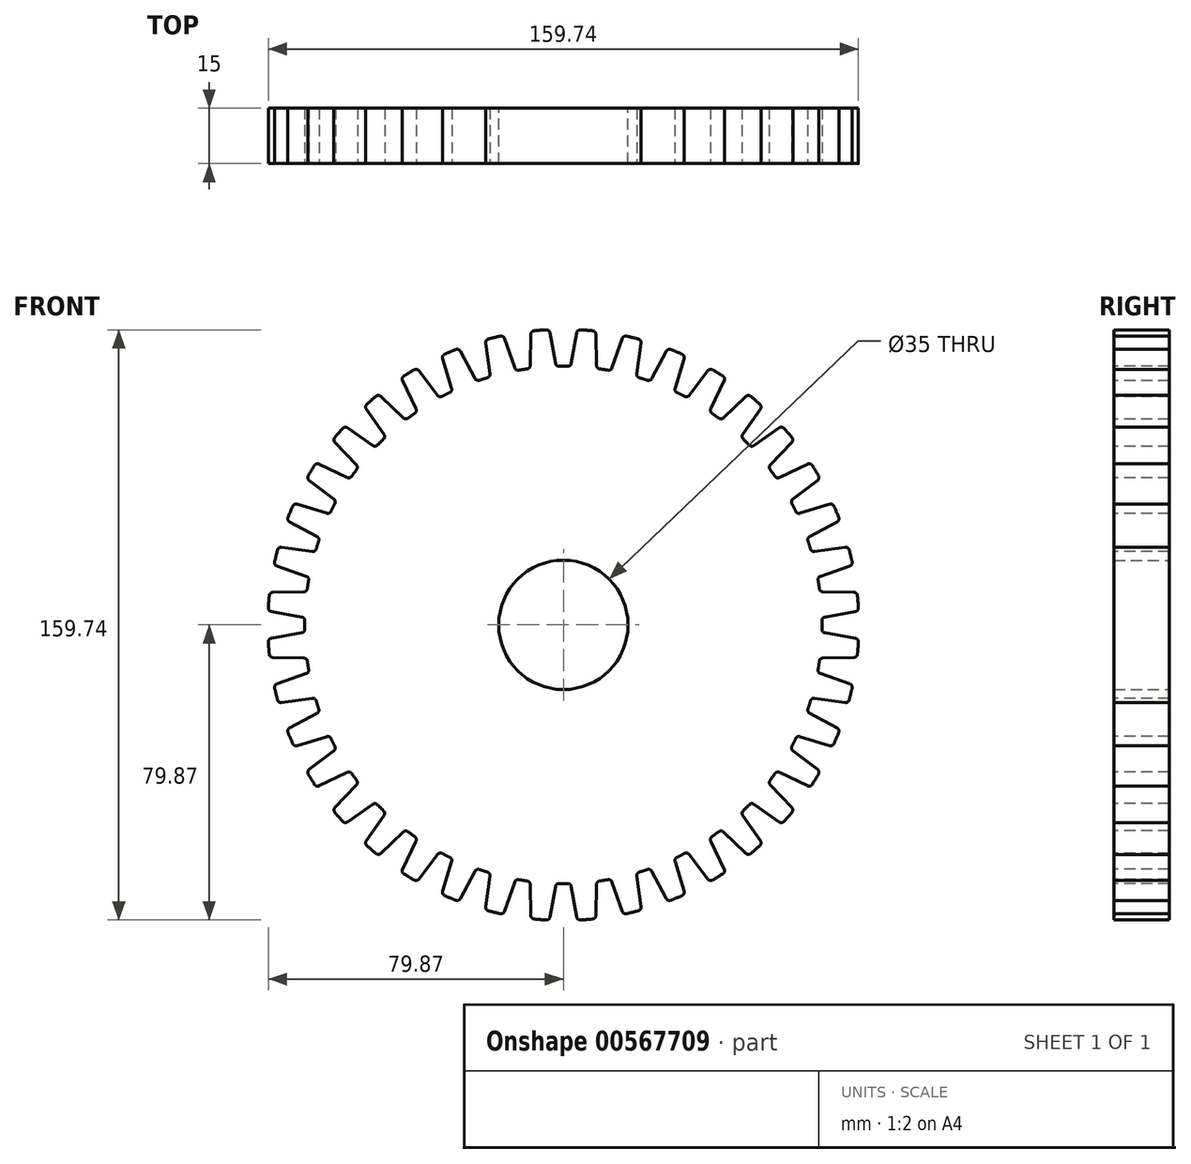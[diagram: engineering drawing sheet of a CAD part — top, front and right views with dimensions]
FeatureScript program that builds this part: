
annotation { "Feature Type Name" : "Feature", "Feature Type Description" : "" }
export const myFeature = defineFeature(function(context is Context, id is Id, definition is map)
    precondition{}
    {
        {
            var Q0;
            Q0=qCreatedBy(makeId("Front.planeOp"),FACE);
            var sketch = newSketch(context, id + "F0", { "sketchPlane" : qUnion([Q0])});
            skCircle(sketch, "E0", {"center": v(0, 0) * mm, "radius": 80 * mm});
            skCircle(sketch, "E1", {"center": v(0, 0) * mm, "radius": 17.5 * mm});
            skSolve(sketch);
        }
        {
            var Q0;
            Q0=makeQuery(id+"F0.imprint","IMPRINT",FACE,{"disambiguationData":[TD([[makeQuery(id+"F0.imprint","IMPRINT",EDGE,{"derivedFrom":sQuery(id+"F0.wireOp",EDGE,"E0")}),1.0]])]});
            extrude(context, id + "F1", {"entities" : qUnion([Q0]), "endBound" : BoundingType.SYMMETRIC, "depth" : 15 * mm, "offsetDistance" : 25 * mm});
        }
        {
            var Q0;
            Q0=qCreatedBy(makeId("Front.planeOp"),FACE);
            var sketch = newSketch(context, id + "F2", { "sketchPlane" : qUnion([Q0])});
            skLineSegment(sketch, "E2", {"start": v(0, 80) * mm, "end": v(0, 70) * mm});
            skArc(sketch, "E3", {"start": v(1.15, 70) * mm, "mid": v(0, 70) * mm, "end": v(-1.15, 70) * mm});
            skLineSegment(sketch, "E4", {"start": v(2.15, 70.82) * mm, "end": v(3.6, 79.04) * mm});
            skLineSegment(sketch, "E5.MirrorCS", {"start": v(-2.15, 70.82) * mm, "end": v(-3.6, 79.04) * mm});
            skPoint(sketch, "E6.orphan", {"position": v(-4.08, 81.74) * mm});
            skPoint(sketch, "E7.orphan", {"position": v(4.08, 81.74) * mm});
            skPoint(sketch, "E8.visualSharp", {"position": v(3.75, 79.91) * mm});
            skArc(sketch, "E8.filletArc", {"start": v(4.64, 79.87) * mm, "mid": v(3.96, 79.65) * mm, "end": v(3.6, 79.04) * mm});
            skPoint(sketch, "E9.visualSharp", {"position": v(-3.75, 79.91) * mm});
            skArc(sketch, "E9.filletArc", {"start": v(-3.6, 79.04) * mm, "mid": v(-3.96, 79.65) * mm, "end": v(-4.64, 79.87) * mm});
            skPoint(sketch, "E10.visualSharp", {"position": v(-2, 69.97) * mm});
            skArc(sketch, "E10.filletArc", {"start": v(-2.15, 70.82) * mm, "mid": v(-1.8, 70.22) * mm, "end": v(-1.15, 70) * mm});
            skPoint(sketch, "E11.visualSharp", {"position": v(2, 69.97) * mm});
            skArc(sketch, "E11.filletArc", {"start": v(1.15, 70) * mm, "mid": v(1.8, 70.22) * mm, "end": v(2.15, 70.82) * mm});
            skArc(sketch, "E12.converted", {"start": v(4.64, 79.87) * mm, "mid": v(0, 80) * mm, "end": v(-4.64, 79.87) * mm});
            skPoint(sketch, "E13.1.0", {"position": v(-16.81, 80.1) * mm});
            skPoint(sketch, "E13.1.1", {"position": v(-8.76, 81.37) * mm});
            skPoint(sketch, "E13.1.2", {"position": v(-12.92, 68.8) * mm});
            skPoint(sketch, "E13.1.3", {"position": v(-8.8, 79.52) * mm});
            skPoint(sketch, "E13.1.4", {"position": v(-16.2, 78.34) * mm});
            skLineSegment(sketch, "E13.1.5", {"start": v(-12.51, 79.02) * mm, "end": v(-10.95, 69.14) * mm});
            skPoint(sketch, "E13.1.6", {"position": v(-8.97, 69.42) * mm});
            skLineSegment(sketch, "E13.1.7", {"start": v(-8.96, 70.28) * mm, "end": v(-8.8, 78.63) * mm});
            skLineSegment(sketch, "E13.1.8", {"start": v(-13.2, 69.6) * mm, "end": v(-15.92, 77.5) * mm});
            skArc(sketch, "E13.1.9", {"start": v(-7.9, 79.6) * mm, "mid": v(-12.51, 79.02) * mm, "end": v(-17.08, 78.16) * mm});
            skArc(sketch, "E13.1.10", {"start": v(-9.82, 69.3) * mm, "mid": v(-10.95, 69.14) * mm, "end": v(-12.08, 68.95) * mm});
            skArc(sketch, "E13.1.11", {"start": v(-13.2, 69.6) * mm, "mid": v(-12.76, 69.07) * mm, "end": v(-12.08, 68.95) * mm});
            skArc(sketch, "E13.1.12", {"start": v(-9.82, 69.3) * mm, "mid": v(-9.2, 69.64) * mm, "end": v(-8.96, 70.28) * mm});
            skArc(sketch, "E13.1.13", {"start": v(-7.9, 79.6) * mm, "mid": v(-8.55, 79.3) * mm, "end": v(-8.8, 78.63) * mm});
            skArc(sketch, "E13.1.14", {"start": v(-15.92, 77.5) * mm, "mid": v(-16.38, 78.05) * mm, "end": v(-17.08, 78.16) * mm});
            skPoint(sketch, "E13.2.0", {"position": v(-29.14, 76.48) * mm});
            skPoint(sketch, "E13.2.1", {"position": v(-21.38, 79) * mm});
            skPoint(sketch, "E13.2.2", {"position": v(-23.52, 65.93) * mm});
            skPoint(sketch, "E13.2.3", {"position": v(-21.13, 77.16) * mm});
            skPoint(sketch, "E13.2.4", {"position": v(-28.26, 74.84) * mm});
            skLineSegment(sketch, "E13.2.5", {"start": v(-24.72, 76.08) * mm, "end": v(-21.63, 66.57) * mm});
            skPoint(sketch, "E13.2.6", {"position": v(-19.72, 67.16) * mm});
            skLineSegment(sketch, "E13.2.7", {"start": v(-19.84, 68.01) * mm, "end": v(-21, 76.28) * mm});
            skLineSegment(sketch, "E13.2.8", {"start": v(-23.93, 66.69) * mm, "end": v(-27.85, 74.06) * mm});
            skArc(sketch, "E13.2.9", {"start": v(-20.26, 77.4) * mm, "mid": v(-24.72, 76.08) * mm, "end": v(-29.1, 74.52) * mm});
            skArc(sketch, "E13.2.10", {"start": v(-20.54, 66.92) * mm, "mid": v(-21.63, 66.57) * mm, "end": v(-22.72, 66.21) * mm});
            skArc(sketch, "E13.2.11", {"start": v(-23.93, 66.69) * mm, "mid": v(-23.41, 66.23) * mm, "end": v(-22.72, 66.21) * mm});
            skArc(sketch, "E13.2.12", {"start": v(-20.54, 66.92) * mm, "mid": v(-19.99, 67.34) * mm, "end": v(-19.84, 68.01) * mm});
            skArc(sketch, "E13.2.13", {"start": v(-20.26, 77.4) * mm, "mid": v(-20.84, 76.98) * mm, "end": v(-21, 76.28) * mm});
            skArc(sketch, "E13.2.14", {"start": v(-27.85, 74.06) * mm, "mid": v(-28.38, 74.53) * mm, "end": v(-29.1, 74.52) * mm});
            skPoint(sketch, "E13.3.0", {"position": v(-40.74, 70.98) * mm});
            skPoint(sketch, "E13.3.1", {"position": v(-33.48, 74.68) * mm});
            skPoint(sketch, "E13.3.2", {"position": v(-33.55, 61.44) * mm});
            skPoint(sketch, "E13.3.3", {"position": v(-32.94, 72.9) * mm});
            skPoint(sketch, "E13.3.4", {"position": v(-39.62, 69.5) * mm});
            skLineSegment(sketch, "E13.3.5", {"start": v(-36.32, 71.28) * mm, "end": v(-31.78, 62.37) * mm});
            skPoint(sketch, "E13.3.6", {"position": v(-29.98, 63.25) * mm});
            skLineSegment(sketch, "E13.3.7", {"start": v(-30.24, 64.07) * mm, "end": v(-32.68, 72.06) * mm});
            skLineSegment(sketch, "E13.3.8", {"start": v(-34.06, 62.12) * mm, "end": v(-39.1, 68.8) * mm});
            skArc(sketch, "E13.3.9", {"start": v(-32.12, 73.27) * mm, "mid": v(-36.32, 71.28) * mm, "end": v(-40.4, 69.05) * mm});
            skArc(sketch, "E13.3.10", {"start": v(-30.75, 62.88) * mm, "mid": v(-31.78, 62.37) * mm, "end": v(-32.8, 61.84) * mm});
            skArc(sketch, "E13.3.11", {"start": v(-34.06, 62.12) * mm, "mid": v(-33.48, 61.75) * mm, "end": v(-32.8, 61.84) * mm});
            skArc(sketch, "E13.3.12", {"start": v(-30.75, 62.88) * mm, "mid": v(-30.27, 63.38) * mm, "end": v(-30.24, 64.07) * mm});
            skArc(sketch, "E13.3.13", {"start": v(-32.12, 73.27) * mm, "mid": v(-32.63, 72.77) * mm, "end": v(-32.68, 72.06) * mm});
            skArc(sketch, "E13.3.14", {"start": v(-39.1, 68.8) * mm, "mid": v(-39.7, 69.17) * mm, "end": v(-40.4, 69.05) * mm});
            skPoint(sketch, "E13.4.0", {"position": v(-51.34, 63.73) * mm});
            skPoint(sketch, "E13.4.1", {"position": v(-44.75, 68.53) * mm});
            skPoint(sketch, "E13.4.2", {"position": v(-42.75, 55.43) * mm});
            skPoint(sketch, "E13.4.3", {"position": v(-43.93, 66.86) * mm});
            skPoint(sketch, "E13.4.4", {"position": v(-50, 62.44) * mm});
            skLineSegment(sketch, "E13.4.5", {"start": v(-47.02, 64.72) * mm, "end": v(-41.14, 56.63) * mm});
            skPoint(sketch, "E13.4.6", {"position": v(-39.51, 57.78) * mm});
            skLineSegment(sketch, "E13.4.7", {"start": v(-39.89, 58.56) * mm, "end": v(-43.55, 66.06) * mm});
            skLineSegment(sketch, "E13.4.8", {"start": v(-43.36, 56.03) * mm, "end": v(-49.37, 61.83) * mm});
            skArc(sketch, "E13.4.9", {"start": v(-43.19, 67.34) * mm, "mid": v(-47.02, 64.72) * mm, "end": v(-50.7, 61.88) * mm});
            skArc(sketch, "E13.4.10", {"start": v(-40.21, 57.3) * mm, "mid": v(-41.14, 56.63) * mm, "end": v(-42.07, 55.95) * mm});
            skArc(sketch, "E13.4.11", {"start": v(-43.36, 56.03) * mm, "mid": v(-42.73, 55.75) * mm, "end": v(-42.07, 55.95) * mm});
            skArc(sketch, "E13.4.12", {"start": v(-40.21, 57.3) * mm, "mid": v(-39.82, 57.87) * mm, "end": v(-39.89, 58.56) * mm});
            skArc(sketch, "E13.4.13", {"start": v(-43.19, 67.34) * mm, "mid": v(-43.61, 66.77) * mm, "end": v(-43.55, 66.06) * mm});
            skArc(sketch, "E13.4.14", {"start": v(-49.37, 61.83) * mm, "mid": v(-50.02, 62.1) * mm, "end": v(-50.7, 61.88) * mm});
            skPoint(sketch, "E13.5.0", {"position": v(-60.68, 54.92) * mm});
            skPoint(sketch, "E13.5.1", {"position": v(-54.92, 60.68) * mm});
            skPoint(sketch, "E13.5.2", {"position": v(-50.9, 48.06) * mm});
            skPoint(sketch, "E13.5.3", {"position": v(-53.85, 59.16) * mm});
            skPoint(sketch, "E13.5.4", {"position": v(-59.16, 53.85) * mm});
            skLineSegment(sketch, "E13.5.5", {"start": v(-56.57, 56.57) * mm, "end": v(-49.5, 49.5) * mm});
            skPoint(sketch, "E13.5.6", {"position": v(-48.06, 50.9) * mm});
            skLineSegment(sketch, "E13.5.7", {"start": v(-48.56, 51.6) * mm, "end": v(-53.35, 58.44) * mm});
            skLineSegment(sketch, "E13.5.8", {"start": v(-51.6, 48.56) * mm, "end": v(-58.44, 53.35) * mm});
            skArc(sketch, "E13.5.9", {"start": v(-53.2, 59.76) * mm, "mid": v(-56.57, 56.57) * mm, "end": v(-59.76, 53.2) * mm});
            skArc(sketch, "E13.5.10", {"start": v(-48.68, 50.3) * mm, "mid": v(-49.5, 49.5) * mm, "end": v(-50.3, 48.68) * mm});
            skArc(sketch, "E13.5.11", {"start": v(-51.6, 48.56) * mm, "mid": v(-50.93, 48.38) * mm, "end": v(-50.3, 48.68) * mm});
            skArc(sketch, "E13.5.12", {"start": v(-48.68, 50.3) * mm, "mid": v(-48.38, 50.93) * mm, "end": v(-48.56, 51.6) * mm});
            skArc(sketch, "E13.5.13", {"start": v(-53.2, 59.76) * mm, "mid": v(-53.52, 59.12) * mm, "end": v(-53.35, 58.44) * mm});
            skArc(sketch, "E13.5.14", {"start": v(-58.44, 53.35) * mm, "mid": v(-59.12, 53.52) * mm, "end": v(-59.76, 53.2) * mm});
            skPoint(sketch, "E13.6.0", {"position": v(-68.53, 44.75) * mm});
            skPoint(sketch, "E13.6.1", {"position": v(-63.73, 51.34) * mm});
            skPoint(sketch, "E13.6.2", {"position": v(-57.78, 39.51) * mm});
            skPoint(sketch, "E13.6.3", {"position": v(-62.44, 50) * mm});
            skPoint(sketch, "E13.6.4", {"position": v(-66.86, 43.93) * mm});
            skLineSegment(sketch, "E13.6.5", {"start": v(-64.72, 47.02) * mm, "end": v(-56.63, 41.14) * mm});
            skPoint(sketch, "E13.6.6", {"position": v(-55.43, 42.75) * mm});
            skLineSegment(sketch, "E13.6.7", {"start": v(-56.03, 43.36) * mm, "end": v(-61.83, 49.37) * mm});
            skLineSegment(sketch, "E13.6.8", {"start": v(-58.56, 39.89) * mm, "end": v(-66.06, 43.55) * mm});
            skArc(sketch, "E13.6.9", {"start": v(-61.88, 50.7) * mm, "mid": v(-64.72, 47.02) * mm, "end": v(-67.34, 43.19) * mm});
            skArc(sketch, "E13.6.10", {"start": v(-55.95, 42.07) * mm, "mid": v(-56.63, 41.14) * mm, "end": v(-57.3, 40.21) * mm});
            skArc(sketch, "E13.6.11", {"start": v(-58.56, 39.89) * mm, "mid": v(-57.87, 39.82) * mm, "end": v(-57.3, 40.21) * mm});
            skArc(sketch, "E13.6.12", {"start": v(-55.95, 42.07) * mm, "mid": v(-55.75, 42.73) * mm, "end": v(-56.03, 43.36) * mm});
            skArc(sketch, "E13.6.13", {"start": v(-61.88, 50.7) * mm, "mid": v(-62.1, 50.02) * mm, "end": v(-61.83, 49.37) * mm});
            skArc(sketch, "E13.6.14", {"start": v(-66.06, 43.55) * mm, "mid": v(-66.77, 43.61) * mm, "end": v(-67.34, 43.19) * mm});
            skPoint(sketch, "E13.7.0", {"position": v(-74.68, 33.48) * mm});
            skPoint(sketch, "E13.7.1", {"position": v(-70.98, 40.74) * mm});
            skPoint(sketch, "E13.7.2", {"position": v(-63.25, 29.98) * mm});
            skPoint(sketch, "E13.7.3", {"position": v(-69.5, 39.62) * mm});
            skPoint(sketch, "E13.7.4", {"position": v(-72.9, 32.94) * mm});
            skLineSegment(sketch, "E13.7.5", {"start": v(-71.28, 36.32) * mm, "end": v(-62.37, 31.78) * mm});
            skPoint(sketch, "E13.7.6", {"position": v(-61.44, 33.55) * mm});
            skLineSegment(sketch, "E13.7.7", {"start": v(-62.12, 34.06) * mm, "end": v(-68.8, 39.1) * mm});
            skLineSegment(sketch, "E13.7.8", {"start": v(-64.07, 30.24) * mm, "end": v(-72.06, 32.68) * mm});
            skArc(sketch, "E13.7.9", {"start": v(-69.05, 40.4) * mm, "mid": v(-71.28, 36.32) * mm, "end": v(-73.27, 32.12) * mm});
            skArc(sketch, "E13.7.10", {"start": v(-61.84, 32.8) * mm, "mid": v(-62.37, 31.78) * mm, "end": v(-62.88, 30.75) * mm});
            skArc(sketch, "E13.7.11", {"start": v(-64.07, 30.24) * mm, "mid": v(-63.38, 30.27) * mm, "end": v(-62.88, 30.75) * mm});
            skArc(sketch, "E13.7.12", {"start": v(-61.84, 32.8) * mm, "mid": v(-61.75, 33.48) * mm, "end": v(-62.12, 34.06) * mm});
            skArc(sketch, "E13.7.13", {"start": v(-69.05, 40.4) * mm, "mid": v(-69.17, 39.7) * mm, "end": v(-68.8, 39.1) * mm});
            skArc(sketch, "E13.7.14", {"start": v(-72.06, 32.68) * mm, "mid": v(-72.77, 32.63) * mm, "end": v(-73.27, 32.12) * mm});
            skPoint(sketch, "E13.8.0", {"position": v(-79, 21.38) * mm});
            skPoint(sketch, "E13.8.1", {"position": v(-76.48, 29.14) * mm});
            skPoint(sketch, "E13.8.2", {"position": v(-67.16, 19.72) * mm});
            skPoint(sketch, "E13.8.3", {"position": v(-74.84, 28.26) * mm});
            skPoint(sketch, "E13.8.4", {"position": v(-77.16, 21.13) * mm});
            skLineSegment(sketch, "E13.8.5", {"start": v(-76.08, 24.72) * mm, "end": v(-66.57, 21.63) * mm});
            skPoint(sketch, "E13.8.6", {"position": v(-65.93, 23.52) * mm});
            skLineSegment(sketch, "E13.8.7", {"start": v(-66.69, 23.93) * mm, "end": v(-74.06, 27.85) * mm});
            skLineSegment(sketch, "E13.8.8", {"start": v(-68.01, 19.84) * mm, "end": v(-76.28, 21) * mm});
            skArc(sketch, "E13.8.9", {"start": v(-74.52, 29.1) * mm, "mid": v(-76.08, 24.72) * mm, "end": v(-77.4, 20.26) * mm});
            skArc(sketch, "E13.8.10", {"start": v(-66.21, 22.72) * mm, "mid": v(-66.57, 21.63) * mm, "end": v(-66.92, 20.54) * mm});
            skArc(sketch, "E13.8.11", {"start": v(-68.01, 19.84) * mm, "mid": v(-67.34, 19.99) * mm, "end": v(-66.92, 20.54) * mm});
            skArc(sketch, "E13.8.12", {"start": v(-66.21, 22.72) * mm, "mid": v(-66.23, 23.41) * mm, "end": v(-66.69, 23.93) * mm});
            skArc(sketch, "E13.8.13", {"start": v(-74.52, 29.1) * mm, "mid": v(-74.53, 28.38) * mm, "end": v(-74.06, 27.85) * mm});
            skArc(sketch, "E13.8.14", {"start": v(-76.28, 21) * mm, "mid": v(-76.98, 20.84) * mm, "end": v(-77.4, 20.26) * mm});
            skPoint(sketch, "E13.9.0", {"position": v(-81.37, 8.76) * mm});
            skPoint(sketch, "E13.9.1", {"position": v(-80.1, 16.81) * mm});
            skPoint(sketch, "E13.9.2", {"position": v(-69.42, 8.97) * mm});
            skPoint(sketch, "E13.9.3", {"position": v(-78.34, 16.2) * mm});
            skPoint(sketch, "E13.9.4", {"position": v(-79.52, 8.8) * mm});
            skLineSegment(sketch, "E13.9.5", {"start": v(-79.02, 12.51) * mm, "end": v(-69.14, 10.95) * mm});
            skPoint(sketch, "E13.9.6", {"position": v(-68.8, 12.92) * mm});
            skLineSegment(sketch, "E13.9.7", {"start": v(-69.6, 13.2) * mm, "end": v(-77.5, 15.92) * mm});
            skLineSegment(sketch, "E13.9.8", {"start": v(-70.28, 8.96) * mm, "end": v(-78.63, 8.8) * mm});
            skArc(sketch, "E13.9.9", {"start": v(-78.16, 17.08) * mm, "mid": v(-79.02, 12.51) * mm, "end": v(-79.6, 7.9) * mm});
            skArc(sketch, "E13.9.10", {"start": v(-68.95, 12.08) * mm, "mid": v(-69.14, 10.95) * mm, "end": v(-69.3, 9.82) * mm});
            skArc(sketch, "E13.9.11", {"start": v(-70.28, 8.96) * mm, "mid": v(-69.64, 9.2) * mm, "end": v(-69.3, 9.82) * mm});
            skArc(sketch, "E13.9.12", {"start": v(-68.95, 12.08) * mm, "mid": v(-69.07, 12.76) * mm, "end": v(-69.6, 13.2) * mm});
            skArc(sketch, "E13.9.13", {"start": v(-78.16, 17.08) * mm, "mid": v(-78.05, 16.38) * mm, "end": v(-77.5, 15.92) * mm});
            skArc(sketch, "E13.9.14", {"start": v(-78.63, 8.8) * mm, "mid": v(-79.3, 8.55) * mm, "end": v(-79.6, 7.9) * mm});
            skPoint(sketch, "E13.10.0", {"position": v(-81.74, -4.08) * mm});
            skPoint(sketch, "E13.10.1", {"position": v(-81.74, 4.08) * mm});
            skPoint(sketch, "E13.10.2", {"position": v(-69.97, -2) * mm});
            skPoint(sketch, "E13.10.3", {"position": v(-79.91, 3.75) * mm});
            skPoint(sketch, "E13.10.4", {"position": v(-79.91, -3.75) * mm});
            skLineSegment(sketch, "E13.10.5", {"start": v(-80, 0) * mm, "end": v(-70, 0) * mm});
            skPoint(sketch, "E13.10.6", {"position": v(-69.97, 2) * mm});
            skLineSegment(sketch, "E13.10.7", {"start": v(-70.82, 2.15) * mm, "end": v(-79.04, 3.6) * mm});
            skLineSegment(sketch, "E13.10.8", {"start": v(-70.82, -2.15) * mm, "end": v(-79.04, -3.6) * mm});
            skArc(sketch, "E13.10.9", {"start": v(-79.87, 4.64) * mm, "mid": v(-80, 0) * mm, "end": v(-79.87, -4.64) * mm});
            skArc(sketch, "E13.10.10", {"start": v(-70, 1.15) * mm, "mid": v(-70, 0) * mm, "end": v(-70, -1.15) * mm});
            skArc(sketch, "E13.10.11", {"start": v(-70.82, -2.15) * mm, "mid": v(-70.22, -1.8) * mm, "end": v(-70, -1.15) * mm});
            skArc(sketch, "E13.10.12", {"start": v(-70, 1.15) * mm, "mid": v(-70.22, 1.8) * mm, "end": v(-70.82, 2.15) * mm});
            skArc(sketch, "E13.10.13", {"start": v(-79.87, 4.64) * mm, "mid": v(-79.65, 3.96) * mm, "end": v(-79.04, 3.6) * mm});
            skArc(sketch, "E13.10.14", {"start": v(-79.04, -3.6) * mm, "mid": v(-79.65, -3.96) * mm, "end": v(-79.87, -4.64) * mm});
            skPoint(sketch, "E13.11.0", {"position": v(-80.1, -16.81) * mm});
            skPoint(sketch, "E13.11.1", {"position": v(-81.37, -8.76) * mm});
            skPoint(sketch, "E13.11.2", {"position": v(-68.8, -12.92) * mm});
            skPoint(sketch, "E13.11.3", {"position": v(-79.52, -8.8) * mm});
            skPoint(sketch, "E13.11.4", {"position": v(-78.34, -16.2) * mm});
            skLineSegment(sketch, "E13.11.5", {"start": v(-79.02, -12.51) * mm, "end": v(-69.14, -10.95) * mm});
            skPoint(sketch, "E13.11.6", {"position": v(-69.42, -8.97) * mm});
            skLineSegment(sketch, "E13.11.7", {"start": v(-70.28, -8.96) * mm, "end": v(-78.63, -8.8) * mm});
            skLineSegment(sketch, "E13.11.8", {"start": v(-69.6, -13.2) * mm, "end": v(-77.5, -15.92) * mm});
            skArc(sketch, "E13.11.9", {"start": v(-79.6, -7.9) * mm, "mid": v(-79.02, -12.51) * mm, "end": v(-78.16, -17.08) * mm});
            skArc(sketch, "E13.11.10", {"start": v(-69.3, -9.82) * mm, "mid": v(-69.14, -10.95) * mm, "end": v(-68.95, -12.08) * mm});
            skArc(sketch, "E13.11.11", {"start": v(-69.6, -13.2) * mm, "mid": v(-69.07, -12.76) * mm, "end": v(-68.95, -12.08) * mm});
            skArc(sketch, "E13.11.12", {"start": v(-69.3, -9.82) * mm, "mid": v(-69.64, -9.2) * mm, "end": v(-70.28, -8.96) * mm});
            skArc(sketch, "E13.11.13", {"start": v(-79.6, -7.9) * mm, "mid": v(-79.3, -8.55) * mm, "end": v(-78.63, -8.8) * mm});
            skArc(sketch, "E13.11.14", {"start": v(-77.5, -15.92) * mm, "mid": v(-78.05, -16.38) * mm, "end": v(-78.16, -17.08) * mm});
            skPoint(sketch, "E13.12.0", {"position": v(-76.48, -29.14) * mm});
            skPoint(sketch, "E13.12.1", {"position": v(-79, -21.38) * mm});
            skPoint(sketch, "E13.12.2", {"position": v(-65.93, -23.52) * mm});
            skPoint(sketch, "E13.12.3", {"position": v(-77.16, -21.13) * mm});
            skPoint(sketch, "E13.12.4", {"position": v(-74.84, -28.26) * mm});
            skLineSegment(sketch, "E13.12.5", {"start": v(-76.08, -24.72) * mm, "end": v(-66.57, -21.63) * mm});
            skPoint(sketch, "E13.12.6", {"position": v(-67.16, -19.72) * mm});
            skLineSegment(sketch, "E13.12.7", {"start": v(-68.01, -19.84) * mm, "end": v(-76.28, -21) * mm});
            skLineSegment(sketch, "E13.12.8", {"start": v(-66.69, -23.93) * mm, "end": v(-74.06, -27.85) * mm});
            skArc(sketch, "E13.12.9", {"start": v(-77.4, -20.26) * mm, "mid": v(-76.08, -24.72) * mm, "end": v(-74.52, -29.1) * mm});
            skArc(sketch, "E13.12.10", {"start": v(-66.92, -20.54) * mm, "mid": v(-66.57, -21.63) * mm, "end": v(-66.21, -22.72) * mm});
            skArc(sketch, "E13.12.11", {"start": v(-66.69, -23.93) * mm, "mid": v(-66.23, -23.41) * mm, "end": v(-66.21, -22.72) * mm});
            skArc(sketch, "E13.12.12", {"start": v(-66.92, -20.54) * mm, "mid": v(-67.34, -19.99) * mm, "end": v(-68.01, -19.84) * mm});
            skArc(sketch, "E13.12.13", {"start": v(-77.4, -20.26) * mm, "mid": v(-76.98, -20.84) * mm, "end": v(-76.28, -21) * mm});
            skArc(sketch, "E13.12.14", {"start": v(-74.06, -27.85) * mm, "mid": v(-74.53, -28.38) * mm, "end": v(-74.52, -29.1) * mm});
            skPoint(sketch, "E13.13.0", {"position": v(-70.98, -40.74) * mm});
            skPoint(sketch, "E13.13.1", {"position": v(-74.68, -33.48) * mm});
            skPoint(sketch, "E13.13.2", {"position": v(-61.44, -33.55) * mm});
            skPoint(sketch, "E13.13.3", {"position": v(-72.9, -32.94) * mm});
            skPoint(sketch, "E13.13.4", {"position": v(-69.5, -39.62) * mm});
            skLineSegment(sketch, "E13.13.5", {"start": v(-71.28, -36.32) * mm, "end": v(-62.37, -31.78) * mm});
            skPoint(sketch, "E13.13.6", {"position": v(-63.25, -29.98) * mm});
            skLineSegment(sketch, "E13.13.7", {"start": v(-64.07, -30.24) * mm, "end": v(-72.06, -32.68) * mm});
            skLineSegment(sketch, "E13.13.8", {"start": v(-62.12, -34.06) * mm, "end": v(-68.8, -39.1) * mm});
            skArc(sketch, "E13.13.9", {"start": v(-73.27, -32.12) * mm, "mid": v(-71.28, -36.32) * mm, "end": v(-69.05, -40.4) * mm});
            skArc(sketch, "E13.13.10", {"start": v(-62.88, -30.75) * mm, "mid": v(-62.37, -31.78) * mm, "end": v(-61.84, -32.8) * mm});
            skArc(sketch, "E13.13.11", {"start": v(-62.12, -34.06) * mm, "mid": v(-61.75, -33.48) * mm, "end": v(-61.84, -32.8) * mm});
            skArc(sketch, "E13.13.12", {"start": v(-62.88, -30.75) * mm, "mid": v(-63.38, -30.27) * mm, "end": v(-64.07, -30.24) * mm});
            skArc(sketch, "E13.13.13", {"start": v(-73.27, -32.12) * mm, "mid": v(-72.77, -32.63) * mm, "end": v(-72.06, -32.68) * mm});
            skArc(sketch, "E13.13.14", {"start": v(-68.8, -39.1) * mm, "mid": v(-69.17, -39.7) * mm, "end": v(-69.05, -40.4) * mm});
            skPoint(sketch, "E13.14.0", {"position": v(-63.73, -51.34) * mm});
            skPoint(sketch, "E13.14.1", {"position": v(-68.53, -44.75) * mm});
            skPoint(sketch, "E13.14.2", {"position": v(-55.43, -42.75) * mm});
            skPoint(sketch, "E13.14.3", {"position": v(-66.86, -43.93) * mm});
            skPoint(sketch, "E13.14.4", {"position": v(-62.44, -50) * mm});
            skLineSegment(sketch, "E13.14.5", {"start": v(-64.72, -47.02) * mm, "end": v(-56.63, -41.14) * mm});
            skPoint(sketch, "E13.14.6", {"position": v(-57.78, -39.51) * mm});
            skLineSegment(sketch, "E13.14.7", {"start": v(-58.56, -39.89) * mm, "end": v(-66.06, -43.55) * mm});
            skLineSegment(sketch, "E13.14.8", {"start": v(-56.03, -43.36) * mm, "end": v(-61.83, -49.37) * mm});
            skArc(sketch, "E13.14.9", {"start": v(-67.34, -43.19) * mm, "mid": v(-64.72, -47.02) * mm, "end": v(-61.88, -50.7) * mm});
            skArc(sketch, "E13.14.10", {"start": v(-57.3, -40.21) * mm, "mid": v(-56.63, -41.14) * mm, "end": v(-55.95, -42.07) * mm});
            skArc(sketch, "E13.14.11", {"start": v(-56.03, -43.36) * mm, "mid": v(-55.75, -42.73) * mm, "end": v(-55.95, -42.07) * mm});
            skArc(sketch, "E13.14.12", {"start": v(-57.3, -40.21) * mm, "mid": v(-57.87, -39.82) * mm, "end": v(-58.56, -39.89) * mm});
            skArc(sketch, "E13.14.13", {"start": v(-67.34, -43.19) * mm, "mid": v(-66.77, -43.61) * mm, "end": v(-66.06, -43.55) * mm});
            skArc(sketch, "E13.14.14", {"start": v(-61.83, -49.37) * mm, "mid": v(-62.1, -50.02) * mm, "end": v(-61.88, -50.7) * mm});
            skPoint(sketch, "E14.0.15.0", {"position": v(-48.06, -50.9) * mm});
            skPoint(sketch, "E14.1.15.0", {"position": v(-60.68, -54.92) * mm});
            skPoint(sketch, "E14.2.15.0", {"position": v(-54.92, -60.68) * mm});
            skPoint(sketch, "E14.3.15.0", {"position": v(-59.16, -53.85) * mm});
            skPoint(sketch, "E14.4.15.0", {"position": v(-53.85, -59.16) * mm});
            skLineSegment(sketch, "E14.5.15.0", {"start": v(-56.57, -56.57) * mm, "end": v(-49.5, -49.5) * mm});
            skPoint(sketch, "E14.8.15.0", {"position": v(-50.9, -48.06) * mm});
            skLineSegment(sketch, "E14.9.15.0", {"start": v(-51.6, -48.56) * mm, "end": v(-58.44, -53.35) * mm});
            skLineSegment(sketch, "E14.12.15.0", {"start": v(-48.56, -51.6) * mm, "end": v(-53.35, -58.44) * mm});
            skArc(sketch, "E14.15.15.0", {"start": v(-59.76, -53.2) * mm, "mid": v(-56.57, -56.57) * mm, "end": v(-53.2, -59.76) * mm});
            skArc(sketch, "E14.19.15.0", {"start": v(-50.3, -48.68) * mm, "mid": v(-49.5, -49.5) * mm, "end": v(-48.68, -50.3) * mm});
            skArc(sketch, "E14.23.15.0", {"start": v(-48.56, -51.6) * mm, "mid": v(-48.38, -50.93) * mm, "end": v(-48.68, -50.3) * mm});
            skArc(sketch, "E14.27.15.0", {"start": v(-50.3, -48.68) * mm, "mid": v(-50.93, -48.38) * mm, "end": v(-51.6, -48.56) * mm});
            skArc(sketch, "E14.31.15.0", {"start": v(-59.76, -53.2) * mm, "mid": v(-59.12, -53.52) * mm, "end": v(-58.44, -53.35) * mm});
            skArc(sketch, "E14.35.15.0", {"start": v(-53.35, -58.44) * mm, "mid": v(-53.52, -59.12) * mm, "end": v(-53.2, -59.76) * mm});
            skPoint(sketch, "E14.0.16.0", {"position": v(-39.51, -57.78) * mm});
            skPoint(sketch, "E14.1.16.0", {"position": v(-51.34, -63.73) * mm});
            skPoint(sketch, "E14.2.16.0", {"position": v(-44.75, -68.53) * mm});
            skPoint(sketch, "E14.3.16.0", {"position": v(-50, -62.44) * mm});
            skPoint(sketch, "E14.4.16.0", {"position": v(-43.93, -66.86) * mm});
            skLineSegment(sketch, "E14.5.16.0", {"start": v(-47.02, -64.72) * mm, "end": v(-41.14, -56.63) * mm});
            skPoint(sketch, "E14.8.16.0", {"position": v(-42.75, -55.43) * mm});
            skLineSegment(sketch, "E14.9.16.0", {"start": v(-43.36, -56.03) * mm, "end": v(-49.37, -61.83) * mm});
            skLineSegment(sketch, "E14.12.16.0", {"start": v(-39.89, -58.56) * mm, "end": v(-43.55, -66.06) * mm});
            skArc(sketch, "E14.15.16.0", {"start": v(-50.7, -61.88) * mm, "mid": v(-47.02, -64.72) * mm, "end": v(-43.19, -67.34) * mm});
            skArc(sketch, "E14.19.16.0", {"start": v(-42.07, -55.95) * mm, "mid": v(-41.14, -56.63) * mm, "end": v(-40.21, -57.3) * mm});
            skArc(sketch, "E14.23.16.0", {"start": v(-39.89, -58.56) * mm, "mid": v(-39.82, -57.87) * mm, "end": v(-40.21, -57.3) * mm});
            skArc(sketch, "E14.27.16.0", {"start": v(-42.07, -55.95) * mm, "mid": v(-42.73, -55.75) * mm, "end": v(-43.36, -56.03) * mm});
            skArc(sketch, "E14.31.16.0", {"start": v(-50.7, -61.88) * mm, "mid": v(-50.02, -62.1) * mm, "end": v(-49.37, -61.83) * mm});
            skArc(sketch, "E14.35.16.0", {"start": v(-43.55, -66.06) * mm, "mid": v(-43.61, -66.77) * mm, "end": v(-43.19, -67.34) * mm});
            skPoint(sketch, "E14.0.17.0", {"position": v(-29.98, -63.25) * mm});
            skPoint(sketch, "E14.1.17.0", {"position": v(-40.74, -70.98) * mm});
            skPoint(sketch, "E14.2.17.0", {"position": v(-33.48, -74.68) * mm});
            skPoint(sketch, "E14.3.17.0", {"position": v(-39.62, -69.5) * mm});
            skPoint(sketch, "E14.4.17.0", {"position": v(-32.94, -72.9) * mm});
            skLineSegment(sketch, "E14.5.17.0", {"start": v(-36.32, -71.28) * mm, "end": v(-31.78, -62.37) * mm});
            skPoint(sketch, "E14.8.17.0", {"position": v(-33.55, -61.44) * mm});
            skLineSegment(sketch, "E14.9.17.0", {"start": v(-34.06, -62.12) * mm, "end": v(-39.1, -68.8) * mm});
            skLineSegment(sketch, "E14.12.17.0", {"start": v(-30.24, -64.07) * mm, "end": v(-32.68, -72.06) * mm});
            skArc(sketch, "E14.15.17.0", {"start": v(-40.4, -69.05) * mm, "mid": v(-36.32, -71.28) * mm, "end": v(-32.12, -73.27) * mm});
            skArc(sketch, "E14.19.17.0", {"start": v(-32.8, -61.84) * mm, "mid": v(-31.78, -62.37) * mm, "end": v(-30.75, -62.88) * mm});
            skArc(sketch, "E14.23.17.0", {"start": v(-30.24, -64.07) * mm, "mid": v(-30.27, -63.38) * mm, "end": v(-30.75, -62.88) * mm});
            skArc(sketch, "E14.27.17.0", {"start": v(-32.8, -61.84) * mm, "mid": v(-33.48, -61.75) * mm, "end": v(-34.06, -62.12) * mm});
            skArc(sketch, "E14.31.17.0", {"start": v(-40.4, -69.05) * mm, "mid": v(-39.7, -69.17) * mm, "end": v(-39.1, -68.8) * mm});
            skArc(sketch, "E14.35.17.0", {"start": v(-32.68, -72.06) * mm, "mid": v(-32.63, -72.77) * mm, "end": v(-32.12, -73.27) * mm});
            skPoint(sketch, "E14.0.18.0", {"position": v(-19.72, -67.16) * mm});
            skPoint(sketch, "E14.1.18.0", {"position": v(-29.14, -76.48) * mm});
            skPoint(sketch, "E14.2.18.0", {"position": v(-21.38, -79) * mm});
            skPoint(sketch, "E14.3.18.0", {"position": v(-28.26, -74.84) * mm});
            skPoint(sketch, "E14.4.18.0", {"position": v(-21.13, -77.16) * mm});
            skLineSegment(sketch, "E14.5.18.0", {"start": v(-24.72, -76.08) * mm, "end": v(-21.63, -66.57) * mm});
            skPoint(sketch, "E14.8.18.0", {"position": v(-23.52, -65.93) * mm});
            skLineSegment(sketch, "E14.9.18.0", {"start": v(-23.93, -66.69) * mm, "end": v(-27.85, -74.06) * mm});
            skLineSegment(sketch, "E14.12.18.0", {"start": v(-19.84, -68.01) * mm, "end": v(-21, -76.28) * mm});
            skArc(sketch, "E14.15.18.0", {"start": v(-29.1, -74.52) * mm, "mid": v(-24.72, -76.08) * mm, "end": v(-20.26, -77.4) * mm});
            skArc(sketch, "E14.19.18.0", {"start": v(-22.72, -66.21) * mm, "mid": v(-21.63, -66.57) * mm, "end": v(-20.54, -66.92) * mm});
            skArc(sketch, "E14.23.18.0", {"start": v(-19.84, -68.01) * mm, "mid": v(-19.99, -67.34) * mm, "end": v(-20.54, -66.92) * mm});
            skArc(sketch, "E14.27.18.0", {"start": v(-22.72, -66.21) * mm, "mid": v(-23.41, -66.23) * mm, "end": v(-23.93, -66.69) * mm});
            skArc(sketch, "E14.31.18.0", {"start": v(-29.1, -74.52) * mm, "mid": v(-28.38, -74.53) * mm, "end": v(-27.85, -74.06) * mm});
            skArc(sketch, "E14.35.18.0", {"start": v(-21, -76.28) * mm, "mid": v(-20.84, -76.98) * mm, "end": v(-20.26, -77.4) * mm});
            skPoint(sketch, "E14.0.19.0", {"position": v(-8.97, -69.42) * mm});
            skPoint(sketch, "E14.1.19.0", {"position": v(-16.81, -80.1) * mm});
            skPoint(sketch, "E14.2.19.0", {"position": v(-8.76, -81.37) * mm});
            skPoint(sketch, "E14.3.19.0", {"position": v(-16.2, -78.34) * mm});
            skPoint(sketch, "E14.4.19.0", {"position": v(-8.8, -79.52) * mm});
            skLineSegment(sketch, "E14.5.19.0", {"start": v(-12.51, -79.02) * mm, "end": v(-10.95, -69.14) * mm});
            skPoint(sketch, "E14.8.19.0", {"position": v(-12.92, -68.8) * mm});
            skLineSegment(sketch, "E14.9.19.0", {"start": v(-13.2, -69.6) * mm, "end": v(-15.92, -77.5) * mm});
            skLineSegment(sketch, "E14.12.19.0", {"start": v(-8.96, -70.28) * mm, "end": v(-8.8, -78.63) * mm});
            skArc(sketch, "E14.15.19.0", {"start": v(-17.08, -78.16) * mm, "mid": v(-12.51, -79.02) * mm, "end": v(-7.9, -79.6) * mm});
            skArc(sketch, "E14.19.19.0", {"start": v(-12.08, -68.95) * mm, "mid": v(-10.95, -69.14) * mm, "end": v(-9.82, -69.3) * mm});
            skArc(sketch, "E14.23.19.0", {"start": v(-8.96, -70.28) * mm, "mid": v(-9.2, -69.64) * mm, "end": v(-9.82, -69.3) * mm});
            skArc(sketch, "E14.27.19.0", {"start": v(-12.08, -68.95) * mm, "mid": v(-12.76, -69.07) * mm, "end": v(-13.2, -69.6) * mm});
            skArc(sketch, "E14.31.19.0", {"start": v(-17.08, -78.16) * mm, "mid": v(-16.38, -78.05) * mm, "end": v(-15.92, -77.5) * mm});
            skArc(sketch, "E14.35.19.0", {"start": v(-8.8, -78.63) * mm, "mid": v(-8.55, -79.3) * mm, "end": v(-7.9, -79.6) * mm});
            skPoint(sketch, "E15.0.20.0", {"position": v(2, -69.97) * mm});
            skPoint(sketch, "E15.1.20.0", {"position": v(-4.08, -81.74) * mm});
            skPoint(sketch, "E15.2.20.0", {"position": v(4.08, -81.74) * mm});
            skPoint(sketch, "E15.3.20.0", {"position": v(-3.75, -79.91) * mm});
            skPoint(sketch, "E15.4.20.0", {"position": v(3.75, -79.91) * mm});
            skLineSegment(sketch, "E15.5.20.0", {"start": v(0, -80) * mm, "end": v(0, -70) * mm});
            skPoint(sketch, "E15.8.20.0", {"position": v(-2, -69.97) * mm});
            skLineSegment(sketch, "E15.9.20.0", {"start": v(-2.15, -70.82) * mm, "end": v(-3.6, -79.04) * mm});
            skLineSegment(sketch, "E15.12.20.0", {"start": v(2.15, -70.82) * mm, "end": v(3.6, -79.04) * mm});
            skArc(sketch, "E15.15.20.0", {"start": v(-4.64, -79.87) * mm, "mid": v(0, -80) * mm, "end": v(4.64, -79.87) * mm});
            skArc(sketch, "E15.19.20.0", {"start": v(-1.15, -70) * mm, "mid": v(0, -70) * mm, "end": v(1.15, -70) * mm});
            skArc(sketch, "E15.23.20.0", {"start": v(2.15, -70.82) * mm, "mid": v(1.8, -70.22) * mm, "end": v(1.15, -70) * mm});
            skArc(sketch, "E15.27.20.0", {"start": v(-1.15, -70) * mm, "mid": v(-1.8, -70.22) * mm, "end": v(-2.15, -70.82) * mm});
            skArc(sketch, "E15.31.20.0", {"start": v(-4.64, -79.87) * mm, "mid": v(-3.96, -79.65) * mm, "end": v(-3.6, -79.04) * mm});
            skArc(sketch, "E15.35.20.0", {"start": v(3.6, -79.04) * mm, "mid": v(3.96, -79.65) * mm, "end": v(4.64, -79.87) * mm});
            skPoint(sketch, "E15.0.21.0", {"position": v(12.92, -68.8) * mm});
            skPoint(sketch, "E15.1.21.0", {"position": v(8.76, -81.37) * mm});
            skPoint(sketch, "E15.2.21.0", {"position": v(16.81, -80.1) * mm});
            skPoint(sketch, "E15.3.21.0", {"position": v(8.8, -79.52) * mm});
            skPoint(sketch, "E15.4.21.0", {"position": v(16.2, -78.34) * mm});
            skLineSegment(sketch, "E15.5.21.0", {"start": v(12.51, -79.02) * mm, "end": v(10.95, -69.14) * mm});
            skPoint(sketch, "E15.8.21.0", {"position": v(8.97, -69.42) * mm});
            skLineSegment(sketch, "E15.9.21.0", {"start": v(8.96, -70.28) * mm, "end": v(8.8, -78.63) * mm});
            skLineSegment(sketch, "E15.12.21.0", {"start": v(13.2, -69.6) * mm, "end": v(15.92, -77.5) * mm});
            skArc(sketch, "E15.15.21.0", {"start": v(7.9, -79.6) * mm, "mid": v(12.51, -79.02) * mm, "end": v(17.08, -78.16) * mm});
            skArc(sketch, "E15.19.21.0", {"start": v(9.82, -69.3) * mm, "mid": v(10.95, -69.14) * mm, "end": v(12.08, -68.95) * mm});
            skArc(sketch, "E15.23.21.0", {"start": v(13.2, -69.6) * mm, "mid": v(12.76, -69.07) * mm, "end": v(12.08, -68.95) * mm});
            skArc(sketch, "E15.27.21.0", {"start": v(9.82, -69.3) * mm, "mid": v(9.2, -69.64) * mm, "end": v(8.96, -70.28) * mm});
            skArc(sketch, "E15.31.21.0", {"start": v(7.9, -79.6) * mm, "mid": v(8.55, -79.3) * mm, "end": v(8.8, -78.63) * mm});
            skArc(sketch, "E15.35.21.0", {"start": v(15.92, -77.5) * mm, "mid": v(16.38, -78.05) * mm, "end": v(17.08, -78.16) * mm});
            skPoint(sketch, "E15.0.22.0", {"position": v(23.52, -65.93) * mm});
            skPoint(sketch, "E15.1.22.0", {"position": v(21.38, -79) * mm});
            skPoint(sketch, "E15.2.22.0", {"position": v(29.14, -76.48) * mm});
            skPoint(sketch, "E15.3.22.0", {"position": v(21.13, -77.16) * mm});
            skPoint(sketch, "E15.4.22.0", {"position": v(28.26, -74.84) * mm});
            skLineSegment(sketch, "E15.5.22.0", {"start": v(24.72, -76.08) * mm, "end": v(21.63, -66.57) * mm});
            skPoint(sketch, "E15.8.22.0", {"position": v(19.72, -67.16) * mm});
            skLineSegment(sketch, "E15.9.22.0", {"start": v(19.84, -68.01) * mm, "end": v(21, -76.28) * mm});
            skLineSegment(sketch, "E15.12.22.0", {"start": v(23.93, -66.69) * mm, "end": v(27.85, -74.06) * mm});
            skArc(sketch, "E15.15.22.0", {"start": v(20.26, -77.4) * mm, "mid": v(24.72, -76.08) * mm, "end": v(29.1, -74.52) * mm});
            skArc(sketch, "E15.19.22.0", {"start": v(20.54, -66.92) * mm, "mid": v(21.63, -66.57) * mm, "end": v(22.72, -66.21) * mm});
            skArc(sketch, "E15.23.22.0", {"start": v(23.93, -66.69) * mm, "mid": v(23.41, -66.23) * mm, "end": v(22.72, -66.21) * mm});
            skArc(sketch, "E15.27.22.0", {"start": v(20.54, -66.92) * mm, "mid": v(19.99, -67.34) * mm, "end": v(19.84, -68.01) * mm});
            skArc(sketch, "E15.31.22.0", {"start": v(20.26, -77.4) * mm, "mid": v(20.84, -76.98) * mm, "end": v(21, -76.28) * mm});
            skArc(sketch, "E15.35.22.0", {"start": v(27.85, -74.06) * mm, "mid": v(28.38, -74.53) * mm, "end": v(29.1, -74.52) * mm});
            skPoint(sketch, "E15.0.23.0", {"position": v(33.55, -61.44) * mm});
            skPoint(sketch, "E15.1.23.0", {"position": v(33.48, -74.68) * mm});
            skPoint(sketch, "E15.2.23.0", {"position": v(40.74, -70.98) * mm});
            skPoint(sketch, "E15.3.23.0", {"position": v(32.94, -72.9) * mm});
            skPoint(sketch, "E15.4.23.0", {"position": v(39.62, -69.5) * mm});
            skLineSegment(sketch, "E15.5.23.0", {"start": v(36.32, -71.28) * mm, "end": v(31.78, -62.37) * mm});
            skPoint(sketch, "E15.8.23.0", {"position": v(29.98, -63.25) * mm});
            skLineSegment(sketch, "E15.9.23.0", {"start": v(30.24, -64.07) * mm, "end": v(32.68, -72.06) * mm});
            skLineSegment(sketch, "E15.12.23.0", {"start": v(34.06, -62.12) * mm, "end": v(39.1, -68.8) * mm});
            skArc(sketch, "E15.15.23.0", {"start": v(32.12, -73.27) * mm, "mid": v(36.32, -71.28) * mm, "end": v(40.4, -69.05) * mm});
            skArc(sketch, "E15.19.23.0", {"start": v(30.75, -62.88) * mm, "mid": v(31.78, -62.37) * mm, "end": v(32.8, -61.84) * mm});
            skArc(sketch, "E15.23.23.0", {"start": v(34.06, -62.12) * mm, "mid": v(33.48, -61.75) * mm, "end": v(32.8, -61.84) * mm});
            skArc(sketch, "E15.27.23.0", {"start": v(30.75, -62.88) * mm, "mid": v(30.27, -63.38) * mm, "end": v(30.24, -64.07) * mm});
            skArc(sketch, "E15.31.23.0", {"start": v(32.12, -73.27) * mm, "mid": v(32.63, -72.77) * mm, "end": v(32.68, -72.06) * mm});
            skArc(sketch, "E15.35.23.0", {"start": v(39.1, -68.8) * mm, "mid": v(39.7, -69.17) * mm, "end": v(40.4, -69.05) * mm});
            skPoint(sketch, "E15.0.24.0", {"position": v(42.75, -55.43) * mm});
            skPoint(sketch, "E15.1.24.0", {"position": v(44.75, -68.53) * mm});
            skPoint(sketch, "E15.2.24.0", {"position": v(51.34, -63.73) * mm});
            skPoint(sketch, "E15.3.24.0", {"position": v(43.93, -66.86) * mm});
            skPoint(sketch, "E15.4.24.0", {"position": v(50, -62.44) * mm});
            skLineSegment(sketch, "E15.5.24.0", {"start": v(47.02, -64.72) * mm, "end": v(41.14, -56.63) * mm});
            skPoint(sketch, "E15.8.24.0", {"position": v(39.51, -57.78) * mm});
            skLineSegment(sketch, "E15.9.24.0", {"start": v(39.89, -58.56) * mm, "end": v(43.55, -66.06) * mm});
            skLineSegment(sketch, "E15.12.24.0", {"start": v(43.36, -56.03) * mm, "end": v(49.37, -61.83) * mm});
            skArc(sketch, "E15.15.24.0", {"start": v(43.19, -67.34) * mm, "mid": v(47.02, -64.72) * mm, "end": v(50.7, -61.88) * mm});
            skArc(sketch, "E15.19.24.0", {"start": v(40.21, -57.3) * mm, "mid": v(41.14, -56.63) * mm, "end": v(42.07, -55.95) * mm});
            skArc(sketch, "E15.23.24.0", {"start": v(43.36, -56.03) * mm, "mid": v(42.73, -55.75) * mm, "end": v(42.07, -55.95) * mm});
            skArc(sketch, "E15.27.24.0", {"start": v(40.21, -57.3) * mm, "mid": v(39.82, -57.87) * mm, "end": v(39.89, -58.56) * mm});
            skArc(sketch, "E15.31.24.0", {"start": v(43.19, -67.34) * mm, "mid": v(43.61, -66.77) * mm, "end": v(43.55, -66.06) * mm});
            skArc(sketch, "E15.35.24.0", {"start": v(49.37, -61.83) * mm, "mid": v(50.02, -62.1) * mm, "end": v(50.7, -61.88) * mm});
            skPoint(sketch, "E16.0.25.0", {"position": v(50.9, -48.06) * mm});
            skPoint(sketch, "E16.1.25.0", {"position": v(54.92, -60.68) * mm});
            skPoint(sketch, "E16.2.25.0", {"position": v(60.68, -54.92) * mm});
            skPoint(sketch, "E16.3.25.0", {"position": v(53.85, -59.16) * mm});
            skPoint(sketch, "E16.4.25.0", {"position": v(59.16, -53.85) * mm});
            skLineSegment(sketch, "E16.5.25.0", {"start": v(56.57, -56.57) * mm, "end": v(49.5, -49.5) * mm});
            skPoint(sketch, "E16.8.25.0", {"position": v(48.06, -50.9) * mm});
            skLineSegment(sketch, "E16.9.25.0", {"start": v(48.56, -51.6) * mm, "end": v(53.35, -58.44) * mm});
            skLineSegment(sketch, "E16.12.25.0", {"start": v(51.6, -48.56) * mm, "end": v(58.44, -53.35) * mm});
            skArc(sketch, "E16.15.25.0", {"start": v(53.2, -59.76) * mm, "mid": v(56.57, -56.57) * mm, "end": v(59.76, -53.2) * mm});
            skArc(sketch, "E16.19.25.0", {"start": v(48.68, -50.3) * mm, "mid": v(49.5, -49.5) * mm, "end": v(50.3, -48.68) * mm});
            skArc(sketch, "E16.23.25.0", {"start": v(51.6, -48.56) * mm, "mid": v(50.93, -48.38) * mm, "end": v(50.3, -48.68) * mm});
            skArc(sketch, "E16.27.25.0", {"start": v(48.68, -50.3) * mm, "mid": v(48.38, -50.93) * mm, "end": v(48.56, -51.6) * mm});
            skArc(sketch, "E16.31.25.0", {"start": v(53.2, -59.76) * mm, "mid": v(53.52, -59.12) * mm, "end": v(53.35, -58.44) * mm});
            skArc(sketch, "E16.35.25.0", {"start": v(58.44, -53.35) * mm, "mid": v(59.12, -53.52) * mm, "end": v(59.76, -53.2) * mm});
            skPoint(sketch, "E16.0.26.0", {"position": v(57.78, -39.51) * mm});
            skPoint(sketch, "E16.1.26.0", {"position": v(63.73, -51.34) * mm});
            skPoint(sketch, "E16.2.26.0", {"position": v(68.53, -44.75) * mm});
            skPoint(sketch, "E16.3.26.0", {"position": v(62.44, -50) * mm});
            skPoint(sketch, "E16.4.26.0", {"position": v(66.86, -43.93) * mm});
            skLineSegment(sketch, "E16.5.26.0", {"start": v(64.72, -47.02) * mm, "end": v(56.63, -41.14) * mm});
            skPoint(sketch, "E16.8.26.0", {"position": v(55.43, -42.75) * mm});
            skLineSegment(sketch, "E16.9.26.0", {"start": v(56.03, -43.36) * mm, "end": v(61.83, -49.37) * mm});
            skLineSegment(sketch, "E16.12.26.0", {"start": v(58.56, -39.89) * mm, "end": v(66.06, -43.55) * mm});
            skArc(sketch, "E16.15.26.0", {"start": v(61.88, -50.7) * mm, "mid": v(64.72, -47.02) * mm, "end": v(67.34, -43.19) * mm});
            skArc(sketch, "E16.19.26.0", {"start": v(55.95, -42.07) * mm, "mid": v(56.63, -41.14) * mm, "end": v(57.3, -40.21) * mm});
            skArc(sketch, "E16.23.26.0", {"start": v(58.56, -39.89) * mm, "mid": v(57.87, -39.82) * mm, "end": v(57.3, -40.21) * mm});
            skArc(sketch, "E16.27.26.0", {"start": v(55.95, -42.07) * mm, "mid": v(55.75, -42.73) * mm, "end": v(56.03, -43.36) * mm});
            skArc(sketch, "E16.31.26.0", {"start": v(61.88, -50.7) * mm, "mid": v(62.1, -50.02) * mm, "end": v(61.83, -49.37) * mm});
            skArc(sketch, "E16.35.26.0", {"start": v(66.06, -43.55) * mm, "mid": v(66.77, -43.61) * mm, "end": v(67.34, -43.19) * mm});
            skPoint(sketch, "E16.0.27.0", {"position": v(63.25, -29.98) * mm});
            skPoint(sketch, "E16.1.27.0", {"position": v(70.98, -40.74) * mm});
            skPoint(sketch, "E16.2.27.0", {"position": v(74.68, -33.48) * mm});
            skPoint(sketch, "E16.3.27.0", {"position": v(69.5, -39.62) * mm});
            skPoint(sketch, "E16.4.27.0", {"position": v(72.9, -32.94) * mm});
            skLineSegment(sketch, "E16.5.27.0", {"start": v(71.28, -36.32) * mm, "end": v(62.37, -31.78) * mm});
            skPoint(sketch, "E16.8.27.0", {"position": v(61.44, -33.55) * mm});
            skLineSegment(sketch, "E16.9.27.0", {"start": v(62.12, -34.06) * mm, "end": v(68.8, -39.1) * mm});
            skLineSegment(sketch, "E16.12.27.0", {"start": v(64.07, -30.24) * mm, "end": v(72.06, -32.68) * mm});
            skArc(sketch, "E16.15.27.0", {"start": v(69.05, -40.4) * mm, "mid": v(71.28, -36.32) * mm, "end": v(73.27, -32.12) * mm});
            skArc(sketch, "E16.19.27.0", {"start": v(61.84, -32.8) * mm, "mid": v(62.37, -31.78) * mm, "end": v(62.88, -30.75) * mm});
            skArc(sketch, "E16.23.27.0", {"start": v(64.07, -30.24) * mm, "mid": v(63.38, -30.27) * mm, "end": v(62.88, -30.75) * mm});
            skArc(sketch, "E16.27.27.0", {"start": v(61.84, -32.8) * mm, "mid": v(61.75, -33.48) * mm, "end": v(62.12, -34.06) * mm});
            skArc(sketch, "E16.31.27.0", {"start": v(69.05, -40.4) * mm, "mid": v(69.17, -39.7) * mm, "end": v(68.8, -39.1) * mm});
            skArc(sketch, "E16.35.27.0", {"start": v(72.06, -32.68) * mm, "mid": v(72.77, -32.63) * mm, "end": v(73.27, -32.12) * mm});
            skPoint(sketch, "E16.0.28.0", {"position": v(67.16, -19.72) * mm});
            skPoint(sketch, "E16.1.28.0", {"position": v(76.48, -29.14) * mm});
            skPoint(sketch, "E16.2.28.0", {"position": v(79, -21.38) * mm});
            skPoint(sketch, "E16.3.28.0", {"position": v(74.84, -28.26) * mm});
            skPoint(sketch, "E16.4.28.0", {"position": v(77.16, -21.13) * mm});
            skLineSegment(sketch, "E16.5.28.0", {"start": v(76.08, -24.72) * mm, "end": v(66.57, -21.63) * mm});
            skPoint(sketch, "E16.8.28.0", {"position": v(65.93, -23.52) * mm});
            skLineSegment(sketch, "E16.9.28.0", {"start": v(66.69, -23.93) * mm, "end": v(74.06, -27.85) * mm});
            skLineSegment(sketch, "E16.12.28.0", {"start": v(68.01, -19.84) * mm, "end": v(76.28, -21) * mm});
            skArc(sketch, "E16.15.28.0", {"start": v(74.52, -29.1) * mm, "mid": v(76.08, -24.72) * mm, "end": v(77.4, -20.26) * mm});
            skArc(sketch, "E16.19.28.0", {"start": v(66.21, -22.72) * mm, "mid": v(66.57, -21.63) * mm, "end": v(66.92, -20.54) * mm});
            skArc(sketch, "E16.23.28.0", {"start": v(68.01, -19.84) * mm, "mid": v(67.34, -19.99) * mm, "end": v(66.92, -20.54) * mm});
            skArc(sketch, "E16.27.28.0", {"start": v(66.21, -22.72) * mm, "mid": v(66.23, -23.41) * mm, "end": v(66.69, -23.93) * mm});
            skArc(sketch, "E16.31.28.0", {"start": v(74.52, -29.1) * mm, "mid": v(74.53, -28.38) * mm, "end": v(74.06, -27.85) * mm});
            skArc(sketch, "E16.35.28.0", {"start": v(76.28, -21) * mm, "mid": v(76.98, -20.84) * mm, "end": v(77.4, -20.26) * mm});
            skPoint(sketch, "E16.0.29.0", {"position": v(69.42, -8.97) * mm});
            skPoint(sketch, "E16.1.29.0", {"position": v(80.1, -16.81) * mm});
            skPoint(sketch, "E16.2.29.0", {"position": v(81.37, -8.76) * mm});
            skPoint(sketch, "E16.3.29.0", {"position": v(78.34, -16.2) * mm});
            skPoint(sketch, "E16.4.29.0", {"position": v(79.52, -8.8) * mm});
            skLineSegment(sketch, "E16.5.29.0", {"start": v(79.02, -12.51) * mm, "end": v(69.14, -10.95) * mm});
            skPoint(sketch, "E16.8.29.0", {"position": v(68.8, -12.92) * mm});
            skLineSegment(sketch, "E16.9.29.0", {"start": v(69.6, -13.2) * mm, "end": v(77.5, -15.92) * mm});
            skLineSegment(sketch, "E16.12.29.0", {"start": v(70.28, -8.96) * mm, "end": v(78.63, -8.8) * mm});
            skArc(sketch, "E16.15.29.0", {"start": v(78.16, -17.08) * mm, "mid": v(79.02, -12.51) * mm, "end": v(79.6, -7.9) * mm});
            skArc(sketch, "E16.19.29.0", {"start": v(68.95, -12.08) * mm, "mid": v(69.14, -10.95) * mm, "end": v(69.3, -9.82) * mm});
            skArc(sketch, "E16.23.29.0", {"start": v(70.28, -8.96) * mm, "mid": v(69.64, -9.2) * mm, "end": v(69.3, -9.82) * mm});
            skArc(sketch, "E16.27.29.0", {"start": v(68.95, -12.08) * mm, "mid": v(69.07, -12.76) * mm, "end": v(69.6, -13.2) * mm});
            skArc(sketch, "E16.31.29.0", {"start": v(78.16, -17.08) * mm, "mid": v(78.05, -16.38) * mm, "end": v(77.5, -15.92) * mm});
            skArc(sketch, "E16.35.29.0", {"start": v(78.63, -8.8) * mm, "mid": v(79.3, -8.55) * mm, "end": v(79.6, -7.9) * mm});
            skPoint(sketch, "E17.0.30.0", {"position": v(69.97, 2) * mm});
            skPoint(sketch, "E17.1.30.0", {"position": v(81.74, -4.08) * mm});
            skPoint(sketch, "E17.2.30.0", {"position": v(81.74, 4.08) * mm});
            skPoint(sketch, "E17.3.30.0", {"position": v(79.91, -3.75) * mm});
            skPoint(sketch, "E17.4.30.0", {"position": v(79.91, 3.75) * mm});
            skLineSegment(sketch, "E17.5.30.0", {"start": v(80, 0) * mm, "end": v(70, 0) * mm});
            skPoint(sketch, "E17.8.30.0", {"position": v(69.97, -2) * mm});
            skLineSegment(sketch, "E17.9.30.0", {"start": v(70.82, -2.15) * mm, "end": v(79.04, -3.6) * mm});
            skLineSegment(sketch, "E17.12.30.0", {"start": v(70.82, 2.15) * mm, "end": v(79.04, 3.6) * mm});
            skArc(sketch, "E17.15.30.0", {"start": v(79.87, -4.64) * mm, "mid": v(80, 0) * mm, "end": v(79.87, 4.64) * mm});
            skArc(sketch, "E17.19.30.0", {"start": v(70, -1.15) * mm, "mid": v(70, 0) * mm, "end": v(70, 1.15) * mm});
            skArc(sketch, "E17.23.30.0", {"start": v(70.82, 2.15) * mm, "mid": v(70.22, 1.8) * mm, "end": v(70, 1.15) * mm});
            skArc(sketch, "E17.27.30.0", {"start": v(70, -1.15) * mm, "mid": v(70.22, -1.8) * mm, "end": v(70.82, -2.15) * mm});
            skArc(sketch, "E17.31.30.0", {"start": v(79.87, -4.64) * mm, "mid": v(79.65, -3.96) * mm, "end": v(79.04, -3.6) * mm});
            skArc(sketch, "E17.35.30.0", {"start": v(79.04, 3.6) * mm, "mid": v(79.65, 3.96) * mm, "end": v(79.87, 4.64) * mm});
            skPoint(sketch, "E17.0.31.0", {"position": v(68.8, 12.92) * mm});
            skPoint(sketch, "E17.1.31.0", {"position": v(81.37, 8.76) * mm});
            skPoint(sketch, "E17.2.31.0", {"position": v(80.1, 16.81) * mm});
            skPoint(sketch, "E17.3.31.0", {"position": v(79.52, 8.8) * mm});
            skPoint(sketch, "E17.4.31.0", {"position": v(78.34, 16.2) * mm});
            skLineSegment(sketch, "E17.5.31.0", {"start": v(79.02, 12.51) * mm, "end": v(69.14, 10.95) * mm});
            skPoint(sketch, "E17.8.31.0", {"position": v(69.42, 8.97) * mm});
            skLineSegment(sketch, "E17.9.31.0", {"start": v(70.28, 8.96) * mm, "end": v(78.63, 8.8) * mm});
            skLineSegment(sketch, "E17.12.31.0", {"start": v(69.6, 13.2) * mm, "end": v(77.5, 15.92) * mm});
            skArc(sketch, "E17.15.31.0", {"start": v(79.6, 7.9) * mm, "mid": v(79.02, 12.51) * mm, "end": v(78.16, 17.08) * mm});
            skArc(sketch, "E17.19.31.0", {"start": v(69.3, 9.82) * mm, "mid": v(69.14, 10.95) * mm, "end": v(68.95, 12.08) * mm});
            skArc(sketch, "E17.23.31.0", {"start": v(69.6, 13.2) * mm, "mid": v(69.07, 12.76) * mm, "end": v(68.95, 12.08) * mm});
            skArc(sketch, "E17.27.31.0", {"start": v(69.3, 9.82) * mm, "mid": v(69.64, 9.2) * mm, "end": v(70.28, 8.96) * mm});
            skArc(sketch, "E17.31.31.0", {"start": v(79.6, 7.9) * mm, "mid": v(79.3, 8.55) * mm, "end": v(78.63, 8.8) * mm});
            skArc(sketch, "E17.35.31.0", {"start": v(77.5, 15.92) * mm, "mid": v(78.05, 16.38) * mm, "end": v(78.16, 17.08) * mm});
            skPoint(sketch, "E18.0.32.0", {"position": v(65.93, 23.52) * mm});
            skPoint(sketch, "E18.1.32.0", {"position": v(79, 21.38) * mm});
            skPoint(sketch, "E18.2.32.0", {"position": v(76.48, 29.14) * mm});
            skPoint(sketch, "E18.3.32.0", {"position": v(77.16, 21.13) * mm});
            skPoint(sketch, "E18.4.32.0", {"position": v(74.84, 28.26) * mm});
            skLineSegment(sketch, "E18.5.32.0", {"start": v(76.08, 24.72) * mm, "end": v(66.57, 21.63) * mm});
            skPoint(sketch, "E18.8.32.0", {"position": v(67.16, 19.72) * mm});
            skLineSegment(sketch, "E18.9.32.0", {"start": v(68.01, 19.84) * mm, "end": v(76.28, 21) * mm});
            skLineSegment(sketch, "E18.12.32.0", {"start": v(66.69, 23.93) * mm, "end": v(74.06, 27.85) * mm});
            skArc(sketch, "E18.15.32.0", {"start": v(77.4, 20.26) * mm, "mid": v(76.08, 24.72) * mm, "end": v(74.52, 29.1) * mm});
            skArc(sketch, "E18.19.32.0", {"start": v(66.92, 20.54) * mm, "mid": v(66.57, 21.63) * mm, "end": v(66.21, 22.72) * mm});
            skArc(sketch, "E18.23.32.0", {"start": v(66.69, 23.93) * mm, "mid": v(66.23, 23.41) * mm, "end": v(66.21, 22.72) * mm});
            skArc(sketch, "E18.27.32.0", {"start": v(66.92, 20.54) * mm, "mid": v(67.34, 19.99) * mm, "end": v(68.01, 19.84) * mm});
            skArc(sketch, "E18.31.32.0", {"start": v(77.4, 20.26) * mm, "mid": v(76.98, 20.84) * mm, "end": v(76.28, 21) * mm});
            skArc(sketch, "E18.35.32.0", {"start": v(74.06, 27.85) * mm, "mid": v(74.53, 28.38) * mm, "end": v(74.52, 29.1) * mm});
            skPoint(sketch, "E18.0.33.0", {"position": v(61.44, 33.55) * mm});
            skPoint(sketch, "E18.1.33.0", {"position": v(74.68, 33.48) * mm});
            skPoint(sketch, "E18.2.33.0", {"position": v(70.98, 40.74) * mm});
            skPoint(sketch, "E18.3.33.0", {"position": v(72.9, 32.94) * mm});
            skPoint(sketch, "E18.4.33.0", {"position": v(69.5, 39.62) * mm});
            skLineSegment(sketch, "E18.5.33.0", {"start": v(71.28, 36.32) * mm, "end": v(62.37, 31.78) * mm});
            skPoint(sketch, "E18.8.33.0", {"position": v(63.25, 29.98) * mm});
            skLineSegment(sketch, "E18.9.33.0", {"start": v(64.07, 30.24) * mm, "end": v(72.06, 32.68) * mm});
            skLineSegment(sketch, "E18.12.33.0", {"start": v(62.12, 34.06) * mm, "end": v(68.8, 39.1) * mm});
            skArc(sketch, "E18.15.33.0", {"start": v(73.27, 32.12) * mm, "mid": v(71.28, 36.32) * mm, "end": v(69.05, 40.4) * mm});
            skArc(sketch, "E18.19.33.0", {"start": v(62.88, 30.75) * mm, "mid": v(62.37, 31.78) * mm, "end": v(61.84, 32.8) * mm});
            skArc(sketch, "E18.23.33.0", {"start": v(62.12, 34.06) * mm, "mid": v(61.75, 33.48) * mm, "end": v(61.84, 32.8) * mm});
            skArc(sketch, "E18.27.33.0", {"start": v(62.88, 30.75) * mm, "mid": v(63.38, 30.27) * mm, "end": v(64.07, 30.24) * mm});
            skArc(sketch, "E18.31.33.0", {"start": v(73.27, 32.12) * mm, "mid": v(72.77, 32.63) * mm, "end": v(72.06, 32.68) * mm});
            skArc(sketch, "E18.35.33.0", {"start": v(68.8, 39.1) * mm, "mid": v(69.17, 39.7) * mm, "end": v(69.05, 40.4) * mm});
            skPoint(sketch, "E18.0.34.0", {"position": v(55.43, 42.75) * mm});
            skPoint(sketch, "E18.1.34.0", {"position": v(68.53, 44.75) * mm});
            skPoint(sketch, "E18.2.34.0", {"position": v(63.73, 51.34) * mm});
            skPoint(sketch, "E18.3.34.0", {"position": v(66.86, 43.93) * mm});
            skPoint(sketch, "E18.4.34.0", {"position": v(62.44, 50) * mm});
            skLineSegment(sketch, "E18.5.34.0", {"start": v(64.72, 47.02) * mm, "end": v(56.63, 41.14) * mm});
            skPoint(sketch, "E18.8.34.0", {"position": v(57.78, 39.51) * mm});
            skLineSegment(sketch, "E18.9.34.0", {"start": v(58.56, 39.89) * mm, "end": v(66.06, 43.55) * mm});
            skLineSegment(sketch, "E18.12.34.0", {"start": v(56.03, 43.36) * mm, "end": v(61.83, 49.37) * mm});
            skArc(sketch, "E18.15.34.0", {"start": v(67.34, 43.19) * mm, "mid": v(64.72, 47.02) * mm, "end": v(61.88, 50.7) * mm});
            skArc(sketch, "E18.19.34.0", {"start": v(57.3, 40.21) * mm, "mid": v(56.63, 41.14) * mm, "end": v(55.95, 42.07) * mm});
            skArc(sketch, "E18.23.34.0", {"start": v(56.03, 43.36) * mm, "mid": v(55.75, 42.73) * mm, "end": v(55.95, 42.07) * mm});
            skArc(sketch, "E18.27.34.0", {"start": v(57.3, 40.21) * mm, "mid": v(57.87, 39.82) * mm, "end": v(58.56, 39.89) * mm});
            skArc(sketch, "E18.31.34.0", {"start": v(67.34, 43.19) * mm, "mid": v(66.77, 43.61) * mm, "end": v(66.06, 43.55) * mm});
            skArc(sketch, "E18.35.34.0", {"start": v(61.83, 49.37) * mm, "mid": v(62.1, 50.02) * mm, "end": v(61.88, 50.7) * mm});
            skPoint(sketch, "E19.0.35.0", {"position": v(48.06, 50.9) * mm});
            skPoint(sketch, "E19.1.35.0", {"position": v(60.68, 54.92) * mm});
            skPoint(sketch, "E19.2.35.0", {"position": v(54.92, 60.68) * mm});
            skPoint(sketch, "E19.3.35.0", {"position": v(59.16, 53.85) * mm});
            skPoint(sketch, "E19.4.35.0", {"position": v(53.85, 59.16) * mm});
            skLineSegment(sketch, "E19.5.35.0", {"start": v(56.57, 56.57) * mm, "end": v(49.5, 49.5) * mm});
            skPoint(sketch, "E19.8.35.0", {"position": v(50.9, 48.06) * mm});
            skLineSegment(sketch, "E19.9.35.0", {"start": v(51.6, 48.56) * mm, "end": v(58.44, 53.35) * mm});
            skLineSegment(sketch, "E19.12.35.0", {"start": v(48.56, 51.6) * mm, "end": v(53.35, 58.44) * mm});
            skArc(sketch, "E19.15.35.0", {"start": v(59.76, 53.2) * mm, "mid": v(56.57, 56.57) * mm, "end": v(53.2, 59.76) * mm});
            skArc(sketch, "E19.19.35.0", {"start": v(50.3, 48.68) * mm, "mid": v(49.5, 49.5) * mm, "end": v(48.68, 50.3) * mm});
            skArc(sketch, "E19.23.35.0", {"start": v(48.56, 51.6) * mm, "mid": v(48.38, 50.93) * mm, "end": v(48.68, 50.3) * mm});
            skArc(sketch, "E19.27.35.0", {"start": v(50.3, 48.68) * mm, "mid": v(50.93, 48.38) * mm, "end": v(51.6, 48.56) * mm});
            skArc(sketch, "E19.31.35.0", {"start": v(59.76, 53.2) * mm, "mid": v(59.12, 53.52) * mm, "end": v(58.44, 53.35) * mm});
            skArc(sketch, "E19.35.35.0", {"start": v(53.35, 58.44) * mm, "mid": v(53.52, 59.12) * mm, "end": v(53.2, 59.76) * mm});
            skPoint(sketch, "E19.0.36.0", {"position": v(39.51, 57.78) * mm});
            skPoint(sketch, "E19.1.36.0", {"position": v(51.34, 63.73) * mm});
            skPoint(sketch, "E19.2.36.0", {"position": v(44.75, 68.53) * mm});
            skPoint(sketch, "E19.3.36.0", {"position": v(50, 62.44) * mm});
            skPoint(sketch, "E19.4.36.0", {"position": v(43.93, 66.86) * mm});
            skLineSegment(sketch, "E19.5.36.0", {"start": v(47.02, 64.72) * mm, "end": v(41.14, 56.63) * mm});
            skPoint(sketch, "E19.8.36.0", {"position": v(42.75, 55.43) * mm});
            skLineSegment(sketch, "E19.9.36.0", {"start": v(43.36, 56.03) * mm, "end": v(49.37, 61.83) * mm});
            skLineSegment(sketch, "E19.12.36.0", {"start": v(39.89, 58.56) * mm, "end": v(43.55, 66.06) * mm});
            skArc(sketch, "E19.15.36.0", {"start": v(50.7, 61.88) * mm, "mid": v(47.02, 64.72) * mm, "end": v(43.19, 67.34) * mm});
            skArc(sketch, "E19.19.36.0", {"start": v(42.07, 55.95) * mm, "mid": v(41.14, 56.63) * mm, "end": v(40.21, 57.3) * mm});
            skArc(sketch, "E19.23.36.0", {"start": v(39.89, 58.56) * mm, "mid": v(39.82, 57.87) * mm, "end": v(40.21, 57.3) * mm});
            skArc(sketch, "E19.27.36.0", {"start": v(42.07, 55.95) * mm, "mid": v(42.73, 55.75) * mm, "end": v(43.36, 56.03) * mm});
            skArc(sketch, "E19.31.36.0", {"start": v(50.7, 61.88) * mm, "mid": v(50.02, 62.1) * mm, "end": v(49.37, 61.83) * mm});
            skArc(sketch, "E19.35.36.0", {"start": v(43.55, 66.06) * mm, "mid": v(43.61, 66.77) * mm, "end": v(43.19, 67.34) * mm});
            skPoint(sketch, "E19.0.37.0", {"position": v(29.98, 63.25) * mm});
            skPoint(sketch, "E19.1.37.0", {"position": v(40.74, 70.98) * mm});
            skPoint(sketch, "E19.2.37.0", {"position": v(33.48, 74.68) * mm});
            skPoint(sketch, "E19.3.37.0", {"position": v(39.62, 69.5) * mm});
            skPoint(sketch, "E19.4.37.0", {"position": v(32.94, 72.9) * mm});
            skLineSegment(sketch, "E19.5.37.0", {"start": v(36.32, 71.28) * mm, "end": v(31.78, 62.37) * mm});
            skPoint(sketch, "E19.8.37.0", {"position": v(33.55, 61.44) * mm});
            skLineSegment(sketch, "E19.9.37.0", {"start": v(34.06, 62.12) * mm, "end": v(39.1, 68.8) * mm});
            skLineSegment(sketch, "E19.12.37.0", {"start": v(30.24, 64.07) * mm, "end": v(32.68, 72.06) * mm});
            skArc(sketch, "E19.15.37.0", {"start": v(40.4, 69.05) * mm, "mid": v(36.32, 71.28) * mm, "end": v(32.12, 73.27) * mm});
            skArc(sketch, "E19.19.37.0", {"start": v(32.8, 61.84) * mm, "mid": v(31.78, 62.37) * mm, "end": v(30.75, 62.88) * mm});
            skArc(sketch, "E19.23.37.0", {"start": v(30.24, 64.07) * mm, "mid": v(30.27, 63.38) * mm, "end": v(30.75, 62.88) * mm});
            skArc(sketch, "E19.27.37.0", {"start": v(32.8, 61.84) * mm, "mid": v(33.48, 61.75) * mm, "end": v(34.06, 62.12) * mm});
            skArc(sketch, "E19.31.37.0", {"start": v(40.4, 69.05) * mm, "mid": v(39.7, 69.17) * mm, "end": v(39.1, 68.8) * mm});
            skArc(sketch, "E19.35.37.0", {"start": v(32.68, 72.06) * mm, "mid": v(32.63, 72.77) * mm, "end": v(32.12, 73.27) * mm});
            skPoint(sketch, "E19.0.38.0", {"position": v(19.72, 67.16) * mm});
            skPoint(sketch, "E19.1.38.0", {"position": v(29.14, 76.48) * mm});
            skPoint(sketch, "E19.2.38.0", {"position": v(21.38, 79) * mm});
            skPoint(sketch, "E19.3.38.0", {"position": v(28.26, 74.84) * mm});
            skPoint(sketch, "E19.4.38.0", {"position": v(21.13, 77.16) * mm});
            skLineSegment(sketch, "E19.5.38.0", {"start": v(24.72, 76.08) * mm, "end": v(21.63, 66.57) * mm});
            skPoint(sketch, "E19.8.38.0", {"position": v(23.52, 65.93) * mm});
            skLineSegment(sketch, "E19.9.38.0", {"start": v(23.93, 66.69) * mm, "end": v(27.85, 74.06) * mm});
            skLineSegment(sketch, "E19.12.38.0", {"start": v(19.84, 68.01) * mm, "end": v(21, 76.28) * mm});
            skArc(sketch, "E19.15.38.0", {"start": v(29.1, 74.52) * mm, "mid": v(24.72, 76.08) * mm, "end": v(20.26, 77.4) * mm});
            skArc(sketch, "E19.19.38.0", {"start": v(22.72, 66.21) * mm, "mid": v(21.63, 66.57) * mm, "end": v(20.54, 66.92) * mm});
            skArc(sketch, "E19.23.38.0", {"start": v(19.84, 68.01) * mm, "mid": v(19.99, 67.34) * mm, "end": v(20.54, 66.92) * mm});
            skArc(sketch, "E19.27.38.0", {"start": v(22.72, 66.21) * mm, "mid": v(23.41, 66.23) * mm, "end": v(23.93, 66.69) * mm});
            skArc(sketch, "E19.31.38.0", {"start": v(29.1, 74.52) * mm, "mid": v(28.38, 74.53) * mm, "end": v(27.85, 74.06) * mm});
            skArc(sketch, "E19.35.38.0", {"start": v(21, 76.28) * mm, "mid": v(20.84, 76.98) * mm, "end": v(20.26, 77.4) * mm});
            skPoint(sketch, "E19.0.39.0", {"position": v(8.97, 69.42) * mm});
            skPoint(sketch, "E19.1.39.0", {"position": v(16.81, 80.1) * mm});
            skPoint(sketch, "E19.2.39.0", {"position": v(8.76, 81.37) * mm});
            skPoint(sketch, "E19.3.39.0", {"position": v(16.2, 78.34) * mm});
            skPoint(sketch, "E19.4.39.0", {"position": v(8.8, 79.52) * mm});
            skLineSegment(sketch, "E19.5.39.0", {"start": v(12.51, 79.02) * mm, "end": v(10.95, 69.14) * mm});
            skPoint(sketch, "E19.8.39.0", {"position": v(12.92, 68.8) * mm});
            skLineSegment(sketch, "E19.9.39.0", {"start": v(13.2, 69.6) * mm, "end": v(15.92, 77.5) * mm});
            skLineSegment(sketch, "E19.12.39.0", {"start": v(8.96, 70.28) * mm, "end": v(8.8, 78.63) * mm});
            skArc(sketch, "E19.15.39.0", {"start": v(17.08, 78.16) * mm, "mid": v(12.51, 79.02) * mm, "end": v(7.9, 79.6) * mm});
            skArc(sketch, "E19.19.39.0", {"start": v(12.08, 68.95) * mm, "mid": v(10.95, 69.14) * mm, "end": v(9.82, 69.3) * mm});
            skArc(sketch, "E19.23.39.0", {"start": v(8.96, 70.28) * mm, "mid": v(9.2, 69.64) * mm, "end": v(9.82, 69.3) * mm});
            skArc(sketch, "E19.27.39.0", {"start": v(12.08, 68.95) * mm, "mid": v(12.76, 69.07) * mm, "end": v(13.2, 69.6) * mm});
            skArc(sketch, "E19.31.39.0", {"start": v(17.08, 78.16) * mm, "mid": v(16.38, 78.05) * mm, "end": v(15.92, 77.5) * mm});
            skArc(sketch, "E19.35.39.0", {"start": v(8.8, 78.63) * mm, "mid": v(8.55, 79.3) * mm, "end": v(7.9, 79.6) * mm});
            skSolve(sketch);
        }
        {
            var Q0;
            Q0 = qSketchRegion(id + "F2", true);
            extrude(context, id + "F3", {"entities" : qUnion([Q0]), "operationType" : NewBodyOperationType.REMOVE, "endBound" : BoundingType.SYMMETRIC, "oppositeDirection" : true, "depth" : 25 * mm, "offsetDistance" : 25 * mm});
        }
    });
